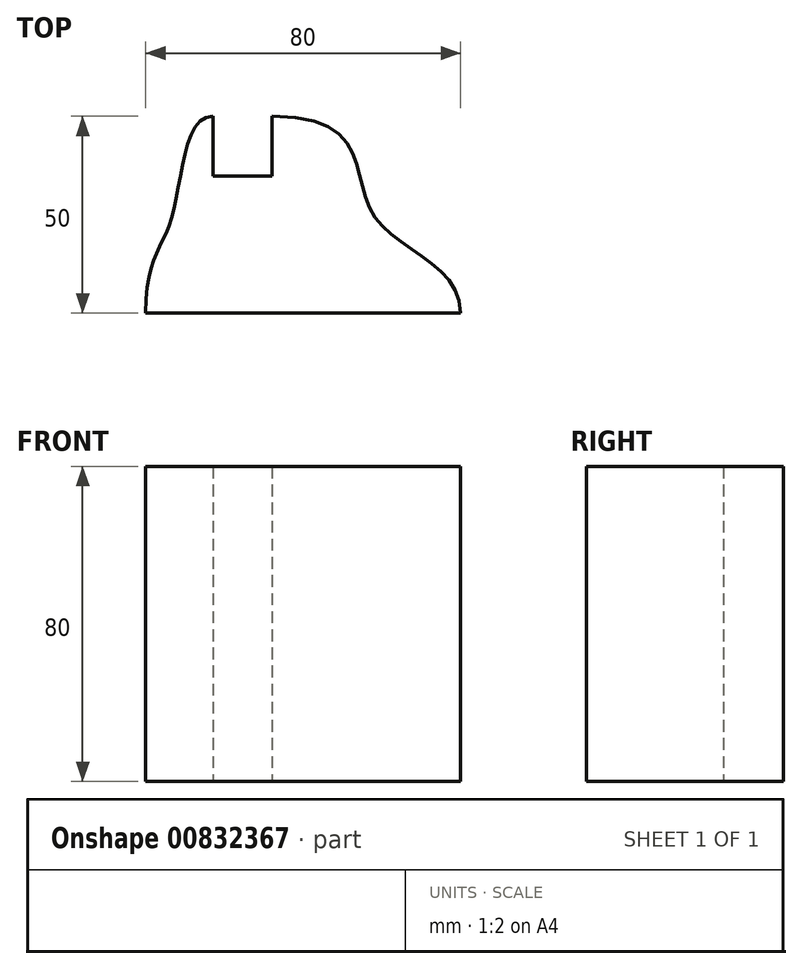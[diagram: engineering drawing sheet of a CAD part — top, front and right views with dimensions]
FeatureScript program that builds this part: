
annotation { "Feature Type Name" : "Feature", "Feature Type Description" : "" }
export const myFeature = defineFeature(function(context is Context, id is Id, definition is map)
    precondition{}
    {
        {
            var Q0;
            Q0=qCreatedBy(makeId("Top.planeOp"),FACE);
            var sketch = newSketch(context, id + "F0", { "sketchPlane" : qUnion([Q0])});
            skLineSegment(sketch, "E0", {"start": v(0, -25) * mm, "end": v(47.9, -25) * mm});
            skLineSegment(sketch, "E1", {"start": v(0, -25) * mm, "end": v(-32.1, -25) * mm});
            skLineSegment(sketch, "E2", {"start": v(-15, 25) * mm, "end": v(-15, 9.8) * mm});
            skLineSegment(sketch, "E3", {"start": v(-15, 9.8) * mm, "end": v(0, 9.8) * mm});
            skLineSegment(sketch, "E4", {"start": v(0, 9.8) * mm, "end": v(0, 25) * mm});
            skFitSpline(sketch, "E5", {"points": [v(0, 25) * mm, v(25.66, 0) * mm, v(47.9, -25) * mm], "startDerivative": vector(151.37, 0) * mm, "endDerivative": vector(0, -76.3) * mm});
            skFitSpline(sketch, "E6", {"points": [v(-15, 25) * mm, v(-25.29, 0) * mm, v(-32.1, -25) * mm], "startDerivative": vector(-44.45, 0) * mm, "endDerivative": vector(0, -86.53) * mm});
            skSolve(sketch);
        }
        {
            var Q0;
            Q0=makeQuery(id+"F0.imprint","IMPRINT",FACE,{"disambiguationData":[TD([[makeQuery(id+"F0.imprint","IMPRINT",EDGE,{"derivedFrom":sQuery(id+"F0.wireOp",EDGE,"E0")}),1.0]])]});
            extrude(context, id + "F1", {"entities" : qUnion([Q0]), "depth" : 80 * mm, "offsetDistance" : 25 * mm});
        }
    });
